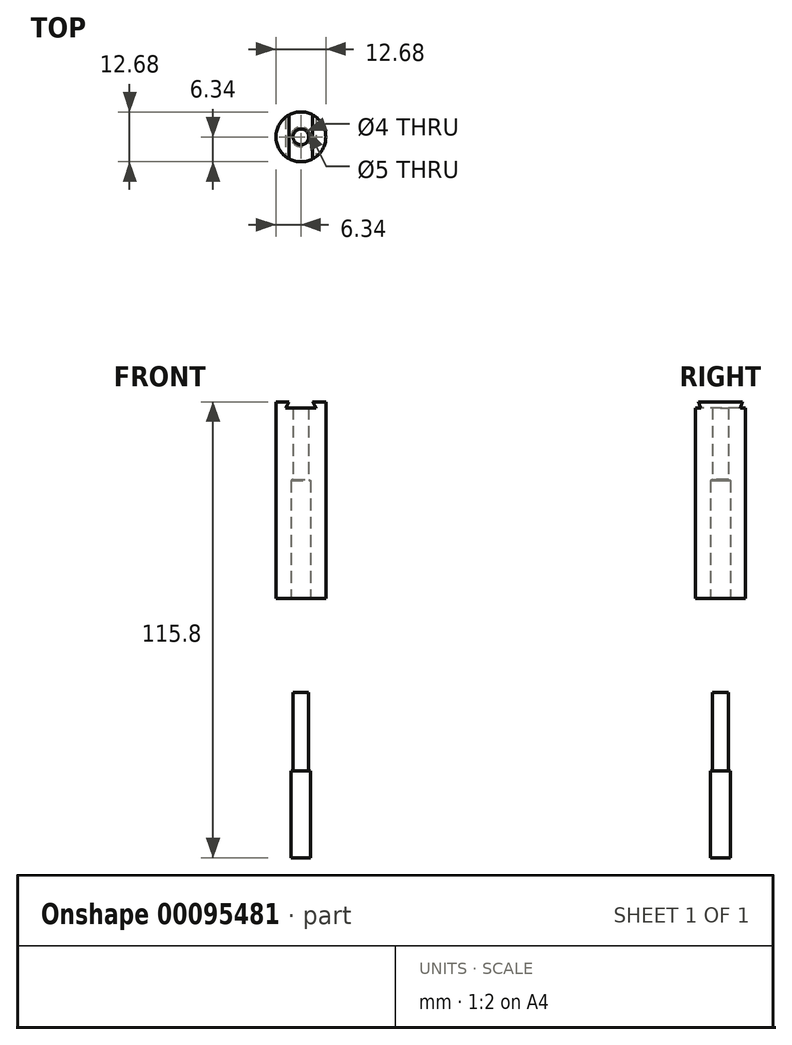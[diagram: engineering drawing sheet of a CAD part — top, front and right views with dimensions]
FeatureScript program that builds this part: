
annotation { "Feature Type Name" : "Feature", "Feature Type Description" : "" }
export const myFeature = defineFeature(function(context is Context, id is Id, definition is map)
    precondition{}
    {
        {
            var Q0;
            Q0=qCreatedBy(makeId("Front.planeOp"),FACE);
            var sketch = newSketch(context, id + "F0", { "sketchPlane" : qUnion([Q0])});
            skLineSegment(sketch, "E0.bottom", {"start": v(0, 0) * mm, "end": v(6.34, 0) * mm});
            skLineSegment(sketch, "E0.top", {"start": v(0, 50) * mm, "end": v(6.34, 50) * mm});
            skLineSegment(sketch, "E0.left", {"start": v(0, 0) * mm, "end": v(0, 50) * mm});
            skLineSegment(sketch, "E0.right", {"start": v(6.34, 0) * mm, "end": v(6.34, 50) * mm});
            skSolve(sketch);
        }
        {
            var Q0;
            Q0 = qSketchRegion(id + "F0", true);
            var Q1;
            Q1=sQuery(id+"F0.wireOp",EDGE,"E0.left");
            revolve(context, id + "F1", {"entities" : qUnion([Q0]), "axis" : qUnion([Q1]), "revolveType" : RevolveType.FULL});
        }
        {
            var Q0;
            Q0=qCreatedBy(makeId("Front.planeOp"),FACE);
            var sketch = newSketch(context, id + "F2", { "sketchPlane" : qUnion([Q0])});
            skLineSegment(sketch, "E1", {"start": v(0, 50) * mm, "end": v(0, 37.29) * mm, "construction": true});
            skLineSegment(sketch, "E2.bottom", {"start": v(3, 51.5) * mm, "end": v(-3, 51.5) * mm});
            skLineSegment(sketch, "E2.top", {"start": v(3, 48.5) * mm, "end": v(-3, 48.5) * mm});
            skLineSegment(sketch, "E2.left", {"start": v(3, 51.5) * mm, "end": v(3, 48.5) * mm});
            skLineSegment(sketch, "E2.right", {"start": v(-3, 51.5) * mm, "end": v(-3, 50) * mm});
            skPoint(sketch, "E2.middle", {"position": v(0, 50) * mm});
            skLineSegment(sketch, "E3", {"start": v(-3, 50) * mm, "end": v(-3.87, 48.5) * mm});
            skLineSegment(sketch, "E4", {"start": v(-3.87, 48.5) * mm, "end": v(-3, 48.5) * mm});
            skLineSegment(sketch, "E5", {"start": v(-3, 50) * mm, "end": v(-3, 48.5) * mm, "construction": true});
            skLineSegment(sketch, "E6.MirrorCS", {"start": v(3, 50) * mm, "end": v(3.87, 48.5) * mm});
            skLineSegment(sketch, "E7.MirrorCS", {"start": v(3.87, 48.5) * mm, "end": v(3, 48.5) * mm});
            skLineSegment(sketch, "E8.MirrorCS", {"start": v(3, 50) * mm, "end": v(3, 48.5) * mm, "construction": true});
            skSolve(sketch);
        }
        {
            var Q0;
            Q0 = qSketchRegion(id + "F2", true);
            extrude(context, id + "F3", {"entities" : qUnion([Q0]), "operationType" : NewBodyOperationType.REMOVE, "endBound" : BoundingType.SYMMETRIC, "oppositeDirection" : true, "depth" : 25 * mm});
        }
        {
            var Q0;
            Q0=makeQuery(id+"F1.opRevolve","SWEPT_FACE",FACE,{"disambiguationData":[OSD([sQuery(id+"F0.wireOp",EDGE,"E0.bottom")])]});
            var sketch = newSketch(context, id + "F4", { "sketchPlane" : qUnion([Q0])});
            skPoint(sketch, "E9", {"position": v(0, 0) * mm});
            skSolve(sketch);
        }
        {
            var Q0;
            Q0=sQuery(id+"F4.wireOp",VERTEX,"E9");
            var Q1;
            Q1=makeQuery(id+"F1.opRevolve","SWEPT_BODY",BODY,{"disambiguationData":[OSD([sQuery(id+"F0.wireOp",EDGE,"E0.bottom"),sQuery(id+"F0.wireOp",EDGE,"E0.top"),sQuery(id+"F0.wireOp",EDGE,"E0.left"),sQuery(id+"F0.wireOp",EDGE,"E0.right")])]});
            hole(context, id + "F5", {"style" : HoleStyle.SIMPLE, "endStyle" : HoleEndStyle.THROUGH, "holeDiameter" : 4 * mm, "locations" : qUnion([Q0]), "scope" : qUnion([Q1]), "isTappedThrough" : true});
        }
        {
            var Q0;
            Q0=sQuery(id+"F4.wireOp",VERTEX,"E9");
            var Q1;
            Q1=makeQuery(id+"F1.opRevolve","SWEPT_BODY",BODY,{"disambiguationData":[OSD([sQuery(id+"F0.wireOp",EDGE,"E0.bottom"),sQuery(id+"F0.wireOp",EDGE,"E0.top"),sQuery(id+"F0.wireOp",EDGE,"E0.left"),sQuery(id+"F0.wireOp",EDGE,"E0.right")])]});
            hole(context, id + "F6", {"style" : HoleStyle.SIMPLE, "endStyle" : HoleEndStyle.BLIND, "holeDiameter" : 5 * mm, "holeDepth" : 30 * mm, "locations" : qUnion([Q0]), "scope" : qUnion([Q1])});
        }
        {
            var Q0;
            Q0=qCreatedBy(makeId("Right.planeOp"),FACE);
            var sketch = newSketch(context, id + "F7", { "sketchPlane" : qUnion([Q0])});
            skLineSegment(sketch, "E10.bottom", {"start": v(0, -23.8) * mm, "end": v(-2, -23.8) * mm});
            skLineSegment(sketch, "E10.top", {"start": v(0, -43.8) * mm, "end": v(-2, -43.8) * mm});
            skLineSegment(sketch, "E10.left", {"start": v(0, -23.8) * mm, "end": v(0, -43.8) * mm});
            skLineSegment(sketch, "E10.right", {"start": v(-2, -23.8) * mm, "end": v(-2, -43.8) * mm});
            skLineSegment(sketch, "E11.bottom", {"start": v(0, -43.8) * mm, "end": v(-2.5, -43.8) * mm});
            skLineSegment(sketch, "E11.top", {"start": v(0, -65.8) * mm, "end": v(-2.5, -65.8) * mm});
            skLineSegment(sketch, "E11.left", {"start": v(0, -43.8) * mm, "end": v(0, -65.8) * mm});
            skLineSegment(sketch, "E11.right", {"start": v(-2.5, -43.8) * mm, "end": v(-2.5, -65.8) * mm});
            skSolve(sketch);
        }
        {
            var Q0;
            Q0 = qSketchRegion(id + "F7", true);
            var Q1;
            Q1=sQuery(id+"F7.wireOp",EDGE,"E10.left");
            revolve(context, id + "F8", {"entities" : qUnion([Q0]), "axis" : qUnion([Q1]), "revolveType" : RevolveType.FULL});
        }
    });
